# Revit family: НЕВАТОМ_Вентилятор VKRS, Версия 2
name_source: partatom
category: Оборудование
revit_build: Autodesk Revit 2017 (Build: 20170118_1100(x64)
units: mm (PartAtom-declared; Revit-internal decimal feet)

## family parameters
Всегда вертикально = Да
На основе рабочей плоскости = Нет
Общий = Нет
При загрузке вырезать с полостями = Нет
Размер круглого соединителя = Использовать диаметр
Тип детали = Нормальный
Точка расчета площади = Нет

## types (42) — shared parameters
ADSK_Единица измерения = шт.
ADSK_Завод-изготовитель = НЕВАТОМ
ADSK_Материал наименование = Оцинкованная сталь
ADSK_Наименование = Вентилятор крышный радиальный с выбросом в сторону
ADSK_Напряжение = 380 В
ADSK_Расход воздуха = 0 м³/ч
Ключевая пометка = Вентиляция
Материал = Сталь ASTM A441
Мощность двигателя N, кВт = 55 кВт

## per-type parameters (varying)
| type | ADSK_Марка | ADSK_Масса | ADSK_Размер_Высота | ADSK_Размер_Длина | ADSK_Размер_Ширина | ADSK_Ток | ADSK_Частота вращения вентилятора | B | D | H | H1 | H2 | H3 | L | L1 | L1-100 | Nevatom_URL | h | h1 | l | l1 | l2 | l3 |
| VKRS № 3,15 АИР63A4 | VKRS-3,15-0,25/1500 | 33.7 | 565 мм | 520 мм | 520 мм | 1 А | 1500 | 440 мм | 315 мм | 565 мм | 339 мм | 288 мм | 322 мм | 520 мм | 620 мм | 520 мм | https://t.me | 20 мм | 17 мм | 420 мм | 210 мм | 252 мм | 357 мм |
| VKRS № 12,5 АИР225M8 | VKRS-12,5-30,0/750 | 853 | 1690 мм | 1650 мм | 1650 мм | 64 А | 750 | 1550 мм | 1250 мм | 1690 мм | 1014 мм | 862 мм | 963 мм | 1650 мм | 2050 мм | 1950 мм | https://t.me | 40 мм | 51 мм | 1550 мм | 775 мм | 930 мм | 1318 мм |
| VKRS № 3,15 АИР80B2 | VKRS-3,15-2,2/3000 | 44 | 565 мм | 520 мм | 520 мм | 5 А | 3000 | 440 мм | 315 мм | 565 мм | 339 мм | 288 мм | 322 мм | 520 мм | 620 мм | 520 мм | https://t.me | 20 мм | 17 мм | 420 мм | 210 мм | 252 мм | 357 мм |
| VKRS № 4 АИР63B6 | VKRS № 4 АИР63B6 | 59 | 690 мм | 625 мм | 625 мм | 1 А | 1000 | 530 мм | 400 мм | 690 мм | 414 мм | 352 мм | 393 мм | 625 мм | 730 мм | 630 мм | https://t.me | 20 мм | 21 мм | 525 мм | 263 мм | 315 мм | 446 мм |
| VKRS № 4 АИР71B4 | VKRS-4,0-0,75/1500 | 60 | 690 мм | 625 мм | 625 мм | 2 А | 1500 | 530 мм | 400 мм | 690 мм | 414 мм | 352 мм | 393 мм | 625 мм | 730 мм | 630 мм | https://t.me | 20 мм | 21 мм | 525 мм | 263 мм | 315 мм | 446 мм |
| VKRS № 4 АИР100L2 | VKRS-4,0-5,5/3000 | 85 | 690 мм | 625 мм | 625 мм | 11 А | 3000 | 530 мм | 400 мм | 690 мм | 414 мм | 352 мм | 393 мм | 625 мм | 730 мм | 630 мм | https://t.me | 20 мм | 21 мм | 525 мм | 263 мм | 315 мм | 446 мм |
| VKRS № 5 АИР80A6 | VKRS-5,0-0,75/1000 | 79.6 | 755 мм | 710 мм | 710 мм | 2 А | 1000 | 630 мм | 500 мм | 755 мм | 453 мм | 385 мм | 430 мм | 710 мм | 860 мм | 760 мм | https://t.me | 20 мм | 23 мм | 610 мм | 305 мм | 366 мм | 519 мм |
| VKRS № 5 АИР90L4 | VKRS-5,0-2,2/1500 | 87 | 755 мм | 710 мм | 710 мм | 5 А | 1500 | 630 мм | 500 мм | 755 мм | 453 мм | 385 мм | 430 мм | 710 мм | 860 мм | 760 мм | https://t.me | 20 мм | 23 мм | 610 мм | 305 мм | 366 мм | 519 мм |
| VKRS № 6,3 АИР100L6 | VKRS-6,3-2,2/1000 | 135.1 | 940 мм | 850 мм | 850 мм | 6 А | 1000 | 755 мм | 630 мм | 940 мм | 564 мм | 479 мм | 536 мм | 850 мм | 1050 мм | 950 мм | https://t.me | 20 мм | 28 мм | 750 мм | 375 мм | 450 мм | 638 мм |
| VKRS № 6,3 АИР132S4 | VKRS-6,3-7,5/1500 | 180 | 940 мм | 850 мм | 850 мм | 16 А | 1500 | 755 мм | 630 мм | 940 мм | 564 мм | 479 мм | 536 мм | 850 мм | 1050 мм | 950 мм | https://t.me | 20 мм | 28 мм | 750 мм | 375 мм | 450 мм | 638 мм |
| VKRS № 8 АИР112MB8 | VKRS-8-3,0/750 | 264.5 | 1260 мм | 1080 мм | 1080 мм | 8 А | 750 | 1005 мм | 800 мм | 1260 мм | 756 мм | 643 мм | 718 мм | 1080 мм | 1355 мм | 1255 мм | https://t.me | 20 мм | 38 мм | 980 мм | 490 мм | 588 мм | 833 мм |
| VKRS № 8 АИР132M6 | VKRS-8,0-7,5/1000 | 297.5 | 1260 мм | 1080 мм | 1080 мм | 17 А | 1000 | 1005 мм | 800 мм | 1260 мм | 756 мм | 643 мм | 718 мм | 1080 мм | 1355 мм | 1255 мм | https://t.me | 20 мм | 38 мм | 980 мм | 490 мм | 588 мм | 833 мм |
| VKRS № 8 АИР180S4 | VKRS-8,0-22,0/1500 | 381 | 1260 мм | 1080 мм | 1080 мм | 43 А | 1500 | 1005 мм | 800 мм | 1260 мм | 756 мм | 643 мм | 718 мм | 1080 мм | 1355 мм | 1255 мм | https://t.me | 20 мм | 38 мм | 980 мм | 490 мм | 588 мм | 833 мм |
| VKRS № 10 АИР160M8 | VKRS-10,0-11/1000 | 520 | 1480 мм | 1500 мм | 1500 мм | 26 А | 750 | 1389 мм | 1000 мм | 1480 мм | 888 мм | 755 мм | 844 мм | 1500 мм | 1800 мм | 1700 мм | https://t.me | 20 мм | 44 мм | 1400 мм | 700 мм | 840 мм | 1190 мм |
| VKRS № 10 АИР200M6 | VKRS-10,0-37,0/1500 | 610 | 1480 мм | 1500 мм | 1500 мм | 44 А | 1000 | 1389 мм | 1000 мм | 1480 мм | 888 мм | 755 мм | 844 мм | 1500 мм | 1800 мм | 1700 мм | https://t.me | 20 мм | 44 мм | 1400 мм | 700 мм | 840 мм | 1190 мм |
| VKRS № 12,5 АИР250М6 | VKRS-12,5-55,0/1000 | 1018 | 1690 мм | 1650 мм | 1650 мм | 104 А | 1000 | 1550 мм | 1250 мм | 1690 мм | 1014 мм | 862 мм | 963 мм | 1650 мм | 2050 мм | 1950 мм | https://t.me | 40 мм | 51 мм | 1550 мм | 775 мм | 930 мм | 1318 мм |
| VKRS № 3,55 АИР63В4 | VKRS-3,55-0,37/1500 | 45.4 | 620 мм | 555 мм | 555 мм | 1 А | 1500 | 480 мм | 355 мм | 620 мм | 372 мм | 316 мм | 353 мм | 555 мм | 703 мм | 603 мм | https://t.me | 20 мм | 19 мм | 455 мм | 228 мм | 273 мм | 387 мм |
| VKRS № 4,5 АИР71А6 | VKRS-4,5-0,37/1000 | 67.9 | 872 мм | 655 мм | 655 мм | 1 А | 1000 | 580 мм | 450 мм | 872 мм | 523 мм | 445 мм | 497 мм | 655 мм | 844 мм | 744 мм | https://t.me | 20 мм | 26 мм | 555 мм | 278 мм | 333 мм | 472 мм |
| VKRS № 5,6 АИР80B6 | VKRS № 5,6 АИР80B6 | 99 | 795 мм | 765 мм | 765 мм | 3 А | 1000 | 690 мм | 560 мм | 795 мм | 477 мм | 405 мм | 453 мм | 765 мм | 1005 мм | 905 мм | https://t.me | 20 мм | 24 мм | 665 мм | 333 мм | 399 мм | 565 мм |
| VKRS № 7,1 АИР112MA8 | VKRS-7,1-2,2/750 | 257.5 | 1227 мм | 920 мм | 920 мм | 6 А | 750 | 840 мм | 710 мм | 1227 мм | 736 мм | 626 мм | 699 мм | 920 мм | 1151 мм | 1051 мм | https://t.me | 20 мм | 37 мм | 820 мм | 410 мм | 492 мм | 697 мм |
| VKRS № 3,15 АИР56А4 | VKRS-3,15-0,12/1500 | 32.4 | 565 мм | 520 мм | 520 мм | 0 А | 1500 | 440 мм | 315 мм | 565 мм | 339 мм | 288 мм | 322 мм | 520 мм | 620 мм | 520 мм | https://t.me | 20 мм | 17 мм | 420 мм | 210 мм | 252 мм | 357 мм |
| VKRS № 3,15 АИР71В2 | VKRS-3,15-1,1/3000 | 38.3 | 565 мм | 520 мм | 520 мм | 3 А | 3000 | 440 мм | 315 мм | 565 мм | 339 мм | 288 мм | 322 мм | 520 мм | 620 мм | 520 мм | https://t.me | 20 мм | 17 мм | 420 мм | 210 мм | 252 мм | 357 мм |
| VKRS № 3,55 АИР90L2 | VKRS-3,55-3/3000 | 60.6 | 620 мм | 555 мм | 555 мм | 1 А | 3000 | 480 мм | 355 мм | 620 мм | 372 мм | 316 мм | 353 мм | 555 мм | 703 мм | 603 мм | https://t.me | 20 мм | 19 мм | 455 мм | 228 мм | 273 мм | 387 мм |
| VKRS № 4.5 АИР80В4 | VKRS-4,5-1,5/1500 | 75.9 | 872 мм | 655 мм | 655 мм | 4 А | 1500 | 580 мм | 450 мм | 872 мм | 523 мм | 445 мм | 497 мм | 655 мм | 844 мм | 744 мм |  | 20 мм | 26 мм | 555 мм | 278 мм | 333 мм | 472 мм |
| VKRS № 4.5 АИР132М2 | VKRS-4,5-11/3000 | 139 | 872 мм | 655 мм | 655 мм | 21 А | 3000 | 580 мм | 450 мм | 872 мм | 523 мм | 445 мм | 497 мм | 655 мм | 844 мм | 744 мм | https://t.me | 20 мм | 26 мм | 555 мм | 278 мм | 333 мм | 472 мм |
| VKRS № 5,6 АИР100L4 | VKRS-5,6-4,0/1500 | 108 | 795 мм | 765 мм | 765 мм | 9 А | 1500 | 690 мм | 560 мм | 795 мм | 477 мм | 405 мм | 453 мм | 765 мм | 1005 мм | 905 мм | https://t.me | 20 мм | 24 мм | 665 мм | 333 мм | 399 мм | 565 мм |
| VKRS № 7,1 АИР112МВ6 | VKRS-7,1-4,0/1000 | 262 | 1227 мм | 920 мм | 920 мм | 9 А | 1000 | 840 мм | 710 мм | 1227 мм | 736 мм | 626 мм | 699 мм | 920 мм | 1151 мм | 1051 мм | https://t.me | 20 мм | 37 мм | 820 мм | 410 мм | 492 мм | 697 мм |
| VKRS № 7,1 АИР160S4 | VKRS-7,1-15,0/1500 | 322 | 1227 мм | 920 мм | 920 мм | 30 А | 1500 | 840 мм | 710 мм | 1227 мм | 736 мм | 626 мм | 699 мм | 920 мм | 1151 мм | 1051 мм | https://t.me | 20 мм | 37 мм | 820 мм | 410 мм | 492 мм | 697 мм |
| VKRS № 4 АИР63В4 | VKRS-4,0-0,37/1500 | 54.6 | 690 мм | 625 мм | 625 мм | 1 А | 1500 | 530 мм | 400 мм | 690 мм | 414 мм | 352 мм | 393 мм | 625 мм | 730 мм | 630 мм | https://t.me | 20 мм | 21 мм | 525 мм | 263 мм | 315 мм | 446 мм |
| VKRS № 4 АИР90L2 | VKRS-4,0-3,0/3000 | 68 | 690 мм | 625 мм | 625 мм | 6 А | 3000 | 530 мм | 400 мм | 690 мм | 414 мм | 352 мм | 393 мм | 625 мм | 730 мм | 630 мм | https://t.me | 20 мм | 21 мм | 525 мм | 263 мм | 315 мм | 446 мм |
| VKRS № 5 АИР71А6 | VKRS-5,0-0,37/1000 | 75.4 | 755 мм | 710 мм | 710 мм | 1 А | 1000 | 630 мм | 500 мм | 755 мм | 453 мм | 385 мм | 430 мм | 710 мм | 860 мм | 760 мм | https://t.me | 20 мм | 23 мм | 610 мм | 305 мм | 366 мм | 519 мм |
| VKRS № 5 АИР80В4 | VKRS-5,0-1,5/1500 | 82 | 755 мм | 710 мм | 710 мм | 4 А | 1500 | 630 мм | 500 мм | 755 мм | 453 мм | 385 мм | 430 мм | 710 мм | 860 мм | 760 мм | https://t.me | 20 мм | 23 мм | 610 мм | 305 мм | 366 мм | 519 мм |
| VKRS № 5 АИР132М2 | VKRS-5,0-11/3000 | 138 | 755 мм | 710 мм | 710 мм | 21 А | 3000 | 630 мм | 500 мм | 755 мм | 453 мм | 385 мм | 430 мм | 710 мм | 860 мм | 760 мм | https://t.me | 20 мм | 23 мм | 610 мм | 305 мм | 366 мм | 519 мм |
| VKRS № 6,3 АИР80В6 | VKRS-6,3-1,1/1000 | 123 | 940 мм | 850 мм | 850 мм | 3 А | 1000 | 755 мм | 630 мм | 940 мм | 564 мм | 479 мм | 536 мм | 850 мм | 1050 мм | 950 мм | https://t.me | 20 мм | 28 мм | 750 мм | 375 мм | 450 мм | 638 мм |
| VKRS № 6,3 АИР100L4 | VKRS-6,3-4,0/1500 | 139 | 940 мм | 850 мм | 850 мм | 9 А | 1500 | 755 мм | 630 мм | 940 мм | 564 мм | 479 мм | 536 мм | 850 мм | 1050 мм | 950 мм | https://t.me | 20 мм | 28 мм | 750 мм | 375 мм | 450 мм | 638 мм |
| VKRS № 8 АИР112MB6 | VKRS-8-4,0/1000 | 264 | 1260 мм | 1080 мм | 1080 мм | 9 А | 1000 | 1005 мм | 800 мм | 1260 мм | 756 мм | 643 мм | 718 мм | 1080 мм | 1355 мм | 1255 мм | https://t.me | 20 мм | 38 мм | 980 мм | 490 мм | 588 мм | 833 мм |
| VKRS № 8 АИР160S4 | VKRS-8,0-15,0/1500 | 318 | 1260 мм | 1080 мм | 1080 мм | 30 А | 1500 | 1005 мм | 800 мм | 1260 мм | 756 мм | 643 мм | 718 мм | 1080 мм | 1355 мм | 1255 мм | https://t.me | 20 мм | 38 мм | 980 мм | 490 мм | 588 мм | 833 мм |
| VKRS № 10 АИР132М8 | VKRS-10-5,5/750 | 461 | 1480 мм | 1500 мм | 1500 мм | 14 А | 750 | 1389 мм | 1000 мм | 1480 мм | 888 мм | 755 мм | 844 мм | 1500 мм | 1800 мм | 1700 мм | https://t.me | 20 мм | 44 мм | 1400 мм | 700 мм | 840 мм | 1190 мм |
| VKRS № 10 АИР160S6 | VKRS-10-11,0/1000 | 490 | 1480 мм | 1500 мм | 1500 мм | 24 А | 1000 | 1389 мм | 1000 мм | 1480 мм | 888 мм | 755 мм | 844 мм | 1500 мм | 1800 мм | 1700 мм | https://t.me | 20 мм | 44 мм | 1400 мм | 700 мм | 840 мм | 1190 мм |
| VKRS № 10 АИР200М4 | VKRS № 10 АИР200М4 | 625 | 1480 мм | 1500 мм | 1500 мм | 69 А | 1500 | 1389 мм | 1000 мм | 1480 мм | 888 мм | 755 мм | 844 мм | 1500 мм | 1800 мм | 1700 мм | https://t.me | 20 мм | 44 мм | 1400 мм | 700 мм | 840 мм | 1190 мм |
| VKRS № 12,5 АИР180М8 | VKRS-12,5-15,0/750 | 728 | 1690 мм | 1650 мм | 1650 мм | 35 А | 750 | 1550 мм | 1250 мм | 1690 мм | 1014 мм | 862 мм | 963 мм | 1650 мм | 2050 мм | 1950 мм | https://t.me | 40 мм | 51 мм | 1550 мм | 775 мм | 930 мм | 1318 мм |
| VKRS № 12,5 АИР225М6 | VKRS-12,5-37,0/1000 | 853 | 1690 мм | 1650 мм | 1650 мм | 71 А | 1000 | 1550 мм | 1250 мм | 1690 мм | 1014 мм | 862 мм | 963 мм | 1650 мм | 2050 мм | 1950 мм | https://t.me | 40 мм | 51 мм | 1550 мм | 775 мм | 930 мм | 1318 мм |
